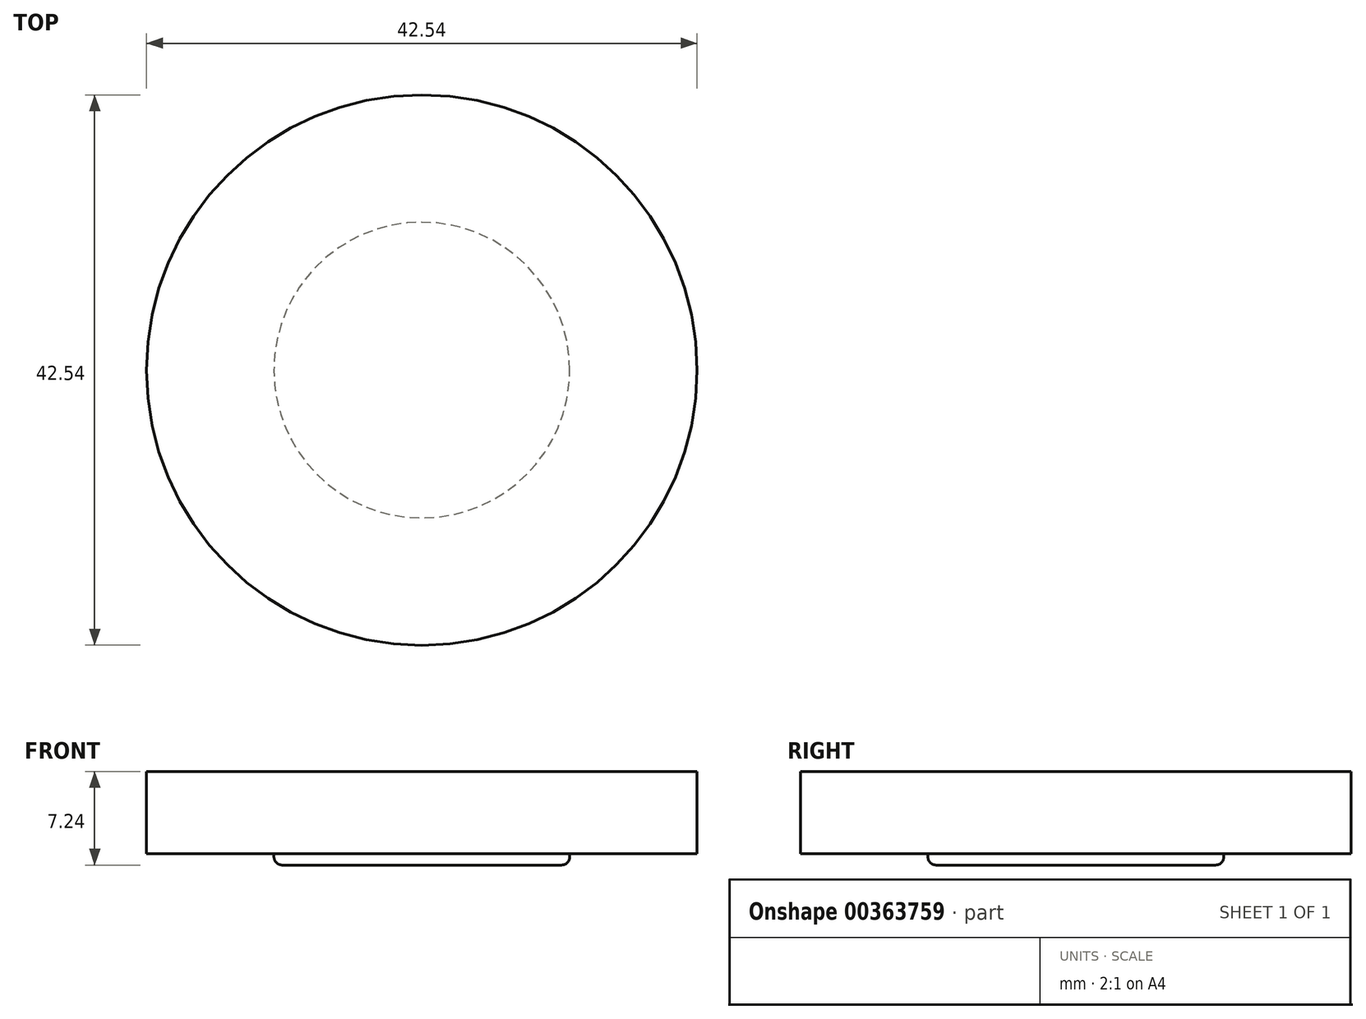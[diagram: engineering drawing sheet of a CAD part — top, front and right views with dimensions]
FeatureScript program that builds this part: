
annotation { "Feature Type Name" : "Feature", "Feature Type Description" : "" }
export const myFeature = defineFeature(function(context is Context, id is Id, definition is map)
    precondition{}
    {
        {
            var Q0;
            Q0=qCreatedBy(makeId("Top.planeOp"),FACE);
            var sketch = newSketch(context, id + "F0", { "sketchPlane" : qUnion([Q0])});
            skCircle(sketch, "E0", {"center": v(0, 0) * mm, "radius": 21.27 * mm});
            skSolve(sketch);
        }
        {
            var Q0;
            Q0 = qSketchRegion(id + "F0", true);
            extrude(context, id + "F1", {"entities" : qUnion([Q0]), "oppositeDirection" : true, "depth" : 3.17 * mm});
        }
        {
            var Q0;
            Q0=makeQuery(id+"F1.opExtrude","CAP_FACE",FACE,{"disambiguationData":[OSD([sQuery(id+"F0.wireOp",EDGE,"E0")])],"isStart":false});
            var sketch = newSketch(context, id + "F2", { "sketchPlane" : qUnion([Q0])});
            skSolve(sketch);
        }
        {
            var Q0;
            Q0 = qSketchRegion(id + "F2", true);
            var Q1;
            Q1=makeQuery(id+"F2.imprint","IMPRINT",FACE,{"disambiguationData":[TD([[makeQuery(id+"F2.imprint","IMPRINT",EDGE,{"derivedFrom":makeQuery(id+"F1.opExtrude","CAP_EDGE",EDGE,{"disambiguationData":[OSD([sQuery(id+"F0.wireOp",EDGE,"E0")])],"isStart":false})}),-1.0]])]});
            extrude(context, id + "F3", {"entities" : qUnion([Q0, Q1]), "operationType" : NewBodyOperationType.ADD, "depth" : 3.17 * mm});
        }
        {
            var Q0;
            Q0=makeQuery(id+"F3.opExtrude","CAP_FACE",FACE,{"disambiguationData":[OSD([sQuery(id+"F0.wireOp",EDGE,"E0")])],"isStart":false});
            var sketch = newSketch(context, id + "F4", { "sketchPlane" : qUnion([Q0])});
            skCircle(sketch, "E1", {"center": v(0, 0) * mm, "radius": 11.43 * mm});
            skSolve(sketch);
        }
        {
            var Q0;
            Q0 = qSketchRegion(id + "F4", true);
            extrude(context, id + "F5", {"entities" : qUnion([Q0]), "operationType" : NewBodyOperationType.ADD, "depth" : 0.89 * mm});
        }
        {
            var Q0;
            Q0=makeQuery(id+"F5.opExtrude","CAP_EDGE",EDGE,{"disambiguationData":[OSD([sQuery(id+"F4.wireOp",EDGE,"E1")])],"isStart":false});
            fillet(context, id + "F6", {"entities" : qUnion([Q0]), "radius" : 0.64 * mm, "tangentPropagation" : true, "allowEdgeOverflow" : false});
        }
    });
